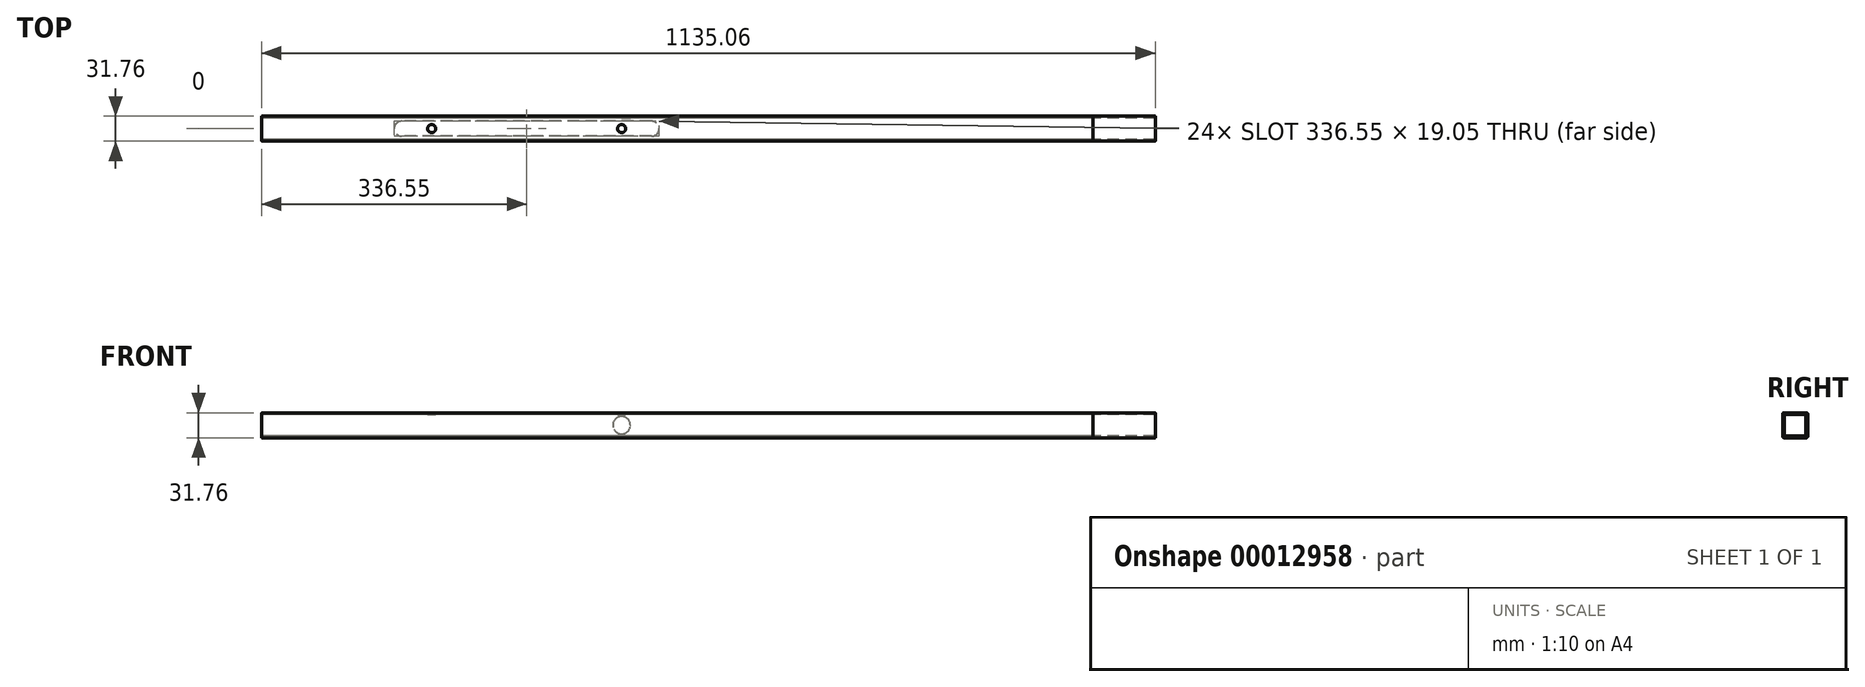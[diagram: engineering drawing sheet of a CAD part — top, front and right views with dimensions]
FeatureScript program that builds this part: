
annotation { "Feature Type Name" : "Feature", "Feature Type Description" : "" }
export const myFeature = defineFeature(function(context is Context, id is Id, definition is map)
    precondition{}
    {
        {
            var Q0;
            Q0=qCreatedBy(makeId("Right.planeOp"),FACE);
            var sketch = newSketch(context, id + "F0", { "sketchPlane" : qUnion([Q0])});
            skLineSegment(sketch, "E0.rect.bottom", {"start": v(14.29, -15.87) * mm, "end": v(-14.29, -15.88) * mm});
            skLineSegment(sketch, "E0.rect.top", {"start": v(14.29, 15.88) * mm, "end": v(-14.29, 15.87) * mm});
            skLineSegment(sketch, "E0.rect.left", {"start": v(15.88, -14.29) * mm, "end": v(15.88, 14.29) * mm});
            skLineSegment(sketch, "E0.rect.right", {"start": v(-15.87, -14.29) * mm, "end": v(-15.88, 14.29) * mm});
            skPoint(sketch, "E0.rect.middle", {"position": v(0, 0) * mm});
            skLineSegment(sketch, "E1.0", {"start": v(13.77, 13.77) * mm, "end": v(-13.77, 13.77) * mm});
            skLineSegment(sketch, "E1.1", {"start": v(13.77, -13.77) * mm, "end": v(13.77, 13.77) * mm});
            skLineSegment(sketch, "E1.2", {"start": v(13.77, -13.77) * mm, "end": v(-13.77, -13.77) * mm});
            skLineSegment(sketch, "E1.3", {"start": v(-13.77, -13.77) * mm, "end": v(-13.77, 13.77) * mm});
            skPoint(sketch, "E2.visualSharp", {"position": v(15.88, -15.87) * mm});
            skArc(sketch, "E2.filletArc", {"start": v(14.29, -15.87) * mm, "mid": v(15.41, -15.41) * mm, "end": v(15.88, -14.29) * mm});
            skPoint(sketch, "E3.visualSharp", {"position": v(-15.88, -15.88) * mm});
            skArc(sketch, "E3.filletArc", {"start": v(-15.87, -14.29) * mm, "mid": v(-15.41, -15.41) * mm, "end": v(-14.29, -15.88) * mm});
            skPoint(sketch, "E4.visualSharp", {"position": v(15.87, 15.88) * mm});
            skArc(sketch, "E4.filletArc", {"start": v(15.88, 14.29) * mm, "mid": v(15.41, 15.41) * mm, "end": v(14.29, 15.88) * mm});
            skPoint(sketch, "E5.visualSharp", {"position": v(-15.88, 15.88) * mm});
            skArc(sketch, "E5.filletArc", {"start": v(-14.29, 15.87) * mm, "mid": v(-15.41, 15.41) * mm, "end": v(-15.88, 14.29) * mm});
            skCircle(sketch, "E6", {"center": v(-6.86, -6.68) * mm, "radius": 3.18 * mm, "construction": true});
            skCircle(sketch, "E7", {"center": v(-0.03, -6.5) * mm, "radius": 3.18 * mm, "construction": true});
            skCircle(sketch, "E8", {"center": v(6.85, -6.57) * mm, "radius": 3.18 * mm, "construction": true});
            skCircle(sketch, "E9", {"center": v(-6.98, 0.37) * mm, "radius": 3.18 * mm, "construction": true});
            skCircle(sketch, "E10", {"center": v(-0.16, 0.24) * mm, "radius": 3.18 * mm, "construction": true});
            skCircle(sketch, "E11", {"center": v(6.65, 0.7) * mm, "radius": 3.18 * mm, "construction": true});
            skCircle(sketch, "E12", {"center": v(-3.8, 6.86) * mm, "radius": 3.18 * mm, "construction": true});
            skCircle(sketch, "E13", {"center": v(3.15, 6.67) * mm, "radius": 3.18 * mm, "construction": true});
            skSolve(sketch);
        }
        {
            var Q0;
            Q0=makeQuery(id+"F0.imprint","IMPRINT",FACE,{"disambiguationData":[TD([[makeQuery(id+"F0.imprint","IMPRINT",EDGE,{"derivedFrom":sQuery(id+"F0.wireOp",EDGE,"E0.rect.bottom")}),-1.0]])]});
            extrude(context, id + "F1", {"entities" : qUnion([Q0]), "depth" : 1135.06 * mm});
        }
        {
            var Q0;
            Q0=makeQuery(id+"F1.opExtrude","SWEPT_FACE",FACE,{"disambiguationData":[OSD([sQuery(id+"F0.wireOp",EDGE,"E0.rect.left")])]});
            var sketch = newSketch(context, id + "F2", { "sketchPlane" : qUnion([Q0])});
            skLineSegment(sketch, "E14", {"start": v(0, 0) * mm, "end": v(-457.2, 0) * mm, "construction": true});
            skSolve(sketch);
        }
        {
            var Q0;
            Q0=qSketchRegion(id+"F0",true);
            extrude(context, id + "F3", {"entities" : qUnion([Q0]), "depth" : 1055.7 * mm});
        }
        {
            var Q0;
            Q0=makeQuery(id+"F1.opExtrude","SWEPT_FACE",FACE,{"disambiguationData":[OSD([sQuery(id+"F0.wireOp",EDGE,"E0.rect.top")])]});
            var sketch = newSketch(context, id + "F4", { "sketchPlane" : qUnion([Q0])});
            skLineSegment(sketch, "E15", {"start": v(0, 0) * mm, "end": v(457.2, 0) * mm, "construction": true});
            skCircle(sketch, "E16", {"center": v(457.2, 0) * mm, "radius": 5.16 * mm});
            skCircle(sketch, "E17", {"center": v(215.9, 0) * mm, "radius": 5.16 * mm});
            skSolve(sketch);
        }
        {
            var Q0;
            Q0=qSketchRegion(id+"F4",true);
            extrude(context, id + "F5", {"entities" : qUnion([Q0]), "operationType" : NewBodyOperationType.REMOVE, "endBound" : BoundingType.UP_TO_NEXT, "oppositeDirection" : true, "depth" : 25.4 * mm});
        }
        {
            var Q0;
            Q0=makeQuery(id+"F1.opExtrude","SWEPT_FACE",FACE,{"disambiguationData":[OSD([sQuery(id+"F0.wireOp",EDGE,"E0.rect.bottom")])]});
            var sketch = newSketch(context, id + "F6", { "sketchPlane" : qUnion([Q0])});
            skLineSegment(sketch, "E18.bottom", {"start": v(495.3, -9.52) * mm, "end": v(177.8, -9.53) * mm});
            skLineSegment(sketch, "E18.top", {"start": v(495.3, 9.52) * mm, "end": v(177.8, 9.52) * mm});
            skLineSegment(sketch, "E18.left", {"start": v(495.3, -9.52) * mm, "end": v(495.3, 9.52) * mm});
            skLineSegment(sketch, "E18.right", {"start": v(177.8, -9.52) * mm, "end": v(177.8, 9.52) * mm});
            skCircle(sketch, "E19", {"center": v(495.3, 0) * mm, "radius": 9.52 * mm});
            skCircle(sketch, "E20", {"center": v(177.8, 0) * mm, "radius": 9.53 * mm});
            skLineSegment(sketch, "E21", {"start": v(0, 0) * mm, "end": v(177.8, 0) * mm, "construction": true});
            skSolve(sketch);
        }
        {
            var Q0;
            {var subQ1=sQuery(id+"F6.wireOp",EDGE,"E18.right");Q0=makeQuery(id+"F6.imprint","IMPRINT",FACE,{"disambiguationData":[TD([[makeQuery(id+"F6.imprint","IMPRINT",EDGE,{"derivedFrom":subQ1}),1.0]])]});}
            var Q1;
            {var subQ1=sQuery(id+"F6.wireOp",EDGE,"E18.right");Q1=makeQuery(id+"F6.imprint","IMPRINT",FACE,{"disambiguationData":[TD([[makeQuery(id+"F6.imprint","IMPRINT",EDGE,{"derivedFrom":subQ1}),-1.0]])]});}
            var Q2;
            {var subQ3=sQuery(id+"F6.wireOp",EDGE,"E18.bottom");Q2=makeQuery(id+"F6.imprint","IMPRINT",FACE,{"disambiguationData":[TD([[makeQuery(id+"F6.imprint","IMPRINT",EDGE,{"derivedFrom":subQ3}),-1.0]])]});}
            var Q3;
            {var subQ1=sQuery(id+"F6.wireOp",EDGE,"E18.left");Q3=makeQuery(id+"F6.imprint","IMPRINT",FACE,{"disambiguationData":[TD([[makeQuery(id+"F6.imprint","IMPRINT",EDGE,{"derivedFrom":subQ1}),1.0]])]});}
            var Q4;
            {var subQ1=sQuery(id+"F6.wireOp",EDGE,"E18.left");Q4=makeQuery(id+"F6.imprint","IMPRINT",FACE,{"disambiguationData":[TD([[makeQuery(id+"F6.imprint","IMPRINT",EDGE,{"derivedFrom":subQ1}),-1.0]])]});}
            extrude(context, id + "F7", {"entities" : qUnion([Q0, Q1, Q2, Q3, Q4]), "operationType" : NewBodyOperationType.REMOVE, "endBound" : BoundingType.UP_TO_NEXT, "oppositeDirection" : true, "depth" : 25.4 * mm});
        }
        {
            var Q0;
            {var subQ0=sQuery(id+"F0.wireOp",EDGE,"E0.rect.left");Q0=makeQuery(id+"F2.imprint","IMPRINT",FACE,{"disambiguationData":[TD([[makeQuery(id+"F2.imprint","IMPRINT",EDGE,{"derivedFrom":makeQuery(id+"F1.opExtrude","CAP_EDGE",EDGE,{"disambiguationData":[OSD([subQ0])],"isStart":true})}),1.0]])]});}
            var sketch = newSketch(context, id + "F8", { "sketchPlane" : qUnion([Q0])});
            skCircle(sketch, "E22", {"center": v(-457.2, 0) * mm, "radius": 11.11 * mm});
            skSolve(sketch);
        }
        {
            var Q0;
            Q0=qSketchRegion(id+"F8",true);
            extrude(context, id + "F9", {"entities" : qUnion([Q0]), "operationType" : NewBodyOperationType.REMOVE, "endBound" : BoundingType.UP_TO_NEXT, "oppositeDirection" : true, "depth" : 25.4 * mm});
        }
    });
